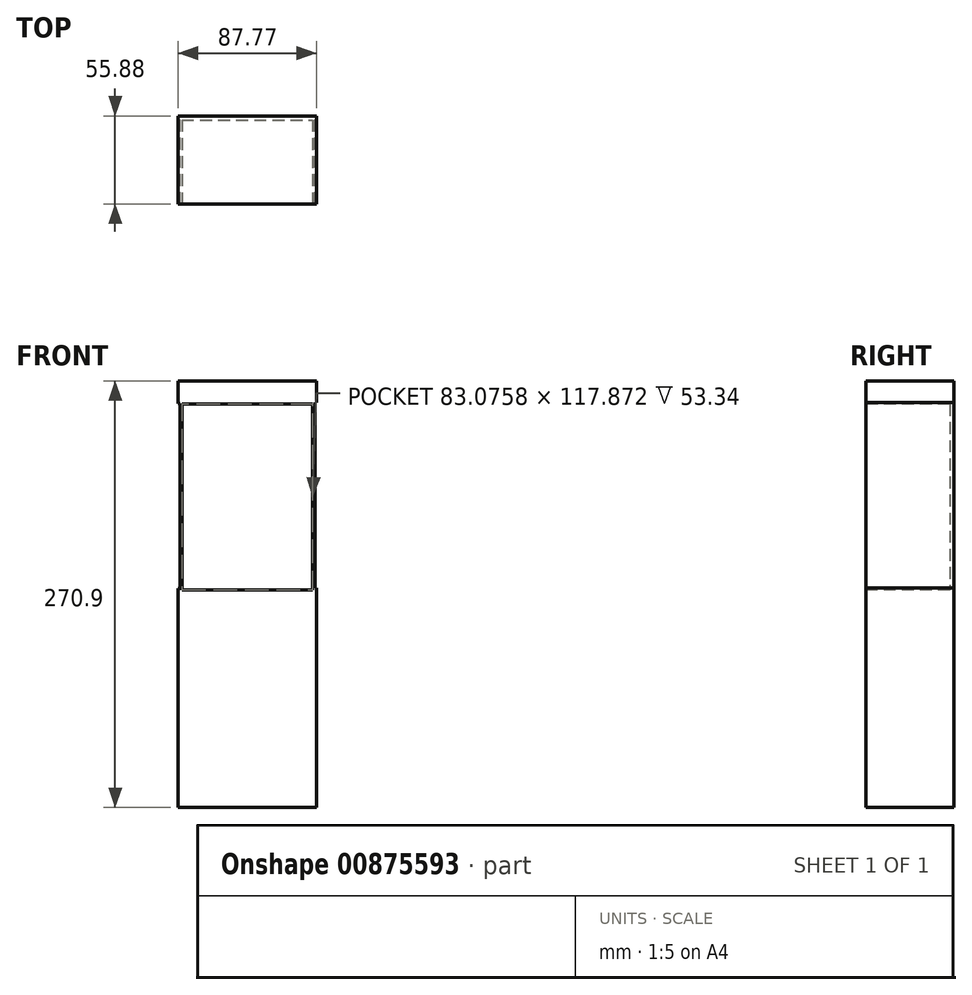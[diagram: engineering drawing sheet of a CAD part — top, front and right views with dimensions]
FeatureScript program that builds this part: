
annotation { "Feature Type Name" : "Feature", "Feature Type Description" : "" }
export const myFeature = defineFeature(function(context is Context, id is Id, definition is map)
    precondition{}
    {
        {
            var Q0;
            Q0=qCreatedBy(makeId("Front.planeOp"),FACE);
            var sketch = newSketch(context, id + "F0", { "sketchPlane" : qUnion([Q0])});
            skLineSegment(sketch, "E0.bottom", {"start": v(-45.98, 95.03) * mm, "end": v(41.79, 95.03) * mm});
            skLineSegment(sketch, "E0.top", {"start": v(-45.98, -175.87) * mm, "end": v(41.79, -175.87) * mm});
            skLineSegment(sketch, "E0.left", {"start": v(-45.98, 95.03) * mm, "end": v(-45.98, -175.87) * mm});
            skLineSegment(sketch, "E0.right", {"start": v(41.79, 95.03) * mm, "end": v(41.79, -175.87) * mm});
            skLineSegment(sketch, "E1.bottom", {"start": v(-43.22, 83.2) * mm, "end": v(39.06, 83.2) * mm});
            skLineSegment(sketch, "E1.top", {"start": v(-43.22, -49.04) * mm, "end": v(39.06, -49.04) * mm});
            skLineSegment(sketch, "E1.left", {"start": v(-43.22, 83.2) * mm, "end": v(-43.22, -49.04) * mm});
            skLineSegment(sketch, "E1.right", {"start": v(39.06, 83.2) * mm, "end": v(39.06, -49.04) * mm});
            skSolve(sketch);
        }
        {
            var Q0;
            Q0=makeQuery(id+"F0.imprint","IMPRINT",FACE,{"disambiguationData":[TD([[makeQuery(id+"F0.imprint","IMPRINT",EDGE,{"derivedFrom":sQuery(id+"F0.wireOp",EDGE,"E1.bottom")}),-1.0]])]});
            var Q1;
            Q1=makeQuery(id+"F0.imprint","IMPRINT",FACE,{"disambiguationData":[TD([[makeQuery(id+"F0.imprint","IMPRINT",EDGE,{"derivedFrom":sQuery(id+"F0.wireOp",EDGE,"E0.bottom")}),-1.0]])]});
            extrude(context, id + "F1", {"entities" : qUnion([Q0, Q1]), "endBound" : BoundingType.SYMMETRIC, "oppositeDirection" : true, "depth" : 55.88 * mm, "offsetDistance" : 25.4 * mm});
        }
        {
            var Q0;
            Q0=makeQuery(id+"F1.opExtrude","CAP_FACE",FACE,{"disambiguationData":[OSD([sQuery(id+"F0.wireOp",EDGE,"E0.bottom"),sQuery(id+"F0.wireOp",EDGE,"E0.top"),sQuery(id+"F0.wireOp",EDGE,"E0.left"),sQuery(id+"F0.wireOp",EDGE,"E0.right")])],"isStart":true});
            var sketch = newSketch(context, id + "F2", { "sketchPlane" : qUnion([Q0])});
            skLineSegment(sketch, "E2.bottom", {"start": v(-43.63, 80.37) * mm, "end": v(39.45, 80.37) * mm});
            skLineSegment(sketch, "E2.top", {"start": v(-43.63, -37.5) * mm, "end": v(39.45, -37.5) * mm});
            skLineSegment(sketch, "E2.left", {"start": v(-43.63, 80.37) * mm, "end": v(-43.63, -37.5) * mm});
            skLineSegment(sketch, "E2.right", {"start": v(39.45, 80.37) * mm, "end": v(39.45, -37.5) * mm});
            skSolve(sketch);
        }
        {
            var Q0;
            Q0=makeQuery(id+"F2.imprint","IMPRINT",FACE,{"disambiguationData":[TD([[makeQuery(id+"F2.imprint","IMPRINT",EDGE,{"derivedFrom":sQuery(id+"F2.wireOp",EDGE,"E2.bottom")}),-1.0]])]});
            extrude(context, id + "F3", {"entities" : qUnion([Q0]), "operationType" : NewBodyOperationType.REMOVE, "oppositeDirection" : true, "depth" : 53.34 * mm, "offsetDistance" : 25.4 * mm});
        }
        {
            var Q0;
            Q0=makeQuery(id+"F1.opExtrude","SWEPT_FACE",FACE,{"disambiguationData":[OSD([sQuery(id+"F0.wireOp",EDGE,"E0.right")])]});
            var sketch = newSketch(context, id + "F4", { "sketchPlane" : qUnion([Q0])});
            skLineSegment(sketch, "E3.bottom", {"start": v(-27.94, 81.35) * mm, "end": v(27.94, 81.35) * mm});
            skLineSegment(sketch, "E3.top", {"start": v(-27.94, -36.5) * mm, "end": v(27.94, -36.5) * mm});
            skLineSegment(sketch, "E3.left", {"start": v(-27.94, 81.35) * mm, "end": v(-27.94, -36.5) * mm});
            skLineSegment(sketch, "E3.right", {"start": v(27.94, 81.35) * mm, "end": v(27.94, -36.5) * mm});
            skSolve(sketch);
        }
        {
            var Q0;
            Q0 = qSketchRegion(id + "F4", true);
            extrude(context, id + "F5", {"entities" : qUnion([Q0]), "operationType" : NewBodyOperationType.REMOVE, "oppositeDirection" : true, "depth" : 1.02 * mm, "offsetDistance" : 25.4 * mm});
        }
        {
            var Q0;
            Q0=makeQuery(id+"F1.opExtrude","SWEPT_FACE",FACE,{"disambiguationData":[OSD([sQuery(id+"F0.wireOp",EDGE,"E0.left")])]});
            var sketch = newSketch(context, id + "F6", { "sketchPlane" : qUnion([Q0])});
            skLineSegment(sketch, "E4.bottom", {"start": v(27.94, 80.81) * mm, "end": v(-27.94, 80.81) * mm});
            skLineSegment(sketch, "E4.top", {"start": v(27.94, -36.8) * mm, "end": v(-27.94, -36.8) * mm});
            skLineSegment(sketch, "E4.left", {"start": v(27.94, 80.81) * mm, "end": v(27.94, -36.8) * mm});
            skLineSegment(sketch, "E4.right", {"start": v(-27.94, 80.81) * mm, "end": v(-27.94, -36.8) * mm});
            skSolve(sketch);
        }
        {
            var Q0;
            Q0 = qSketchRegion(id + "F6", true);
            extrude(context, id + "F7", {"entities" : qUnion([Q0]), "operationType" : NewBodyOperationType.REMOVE, "oppositeDirection" : true, "depth" : 1.02 * mm, "offsetDistance" : 25.4 * mm});
        }
    });
